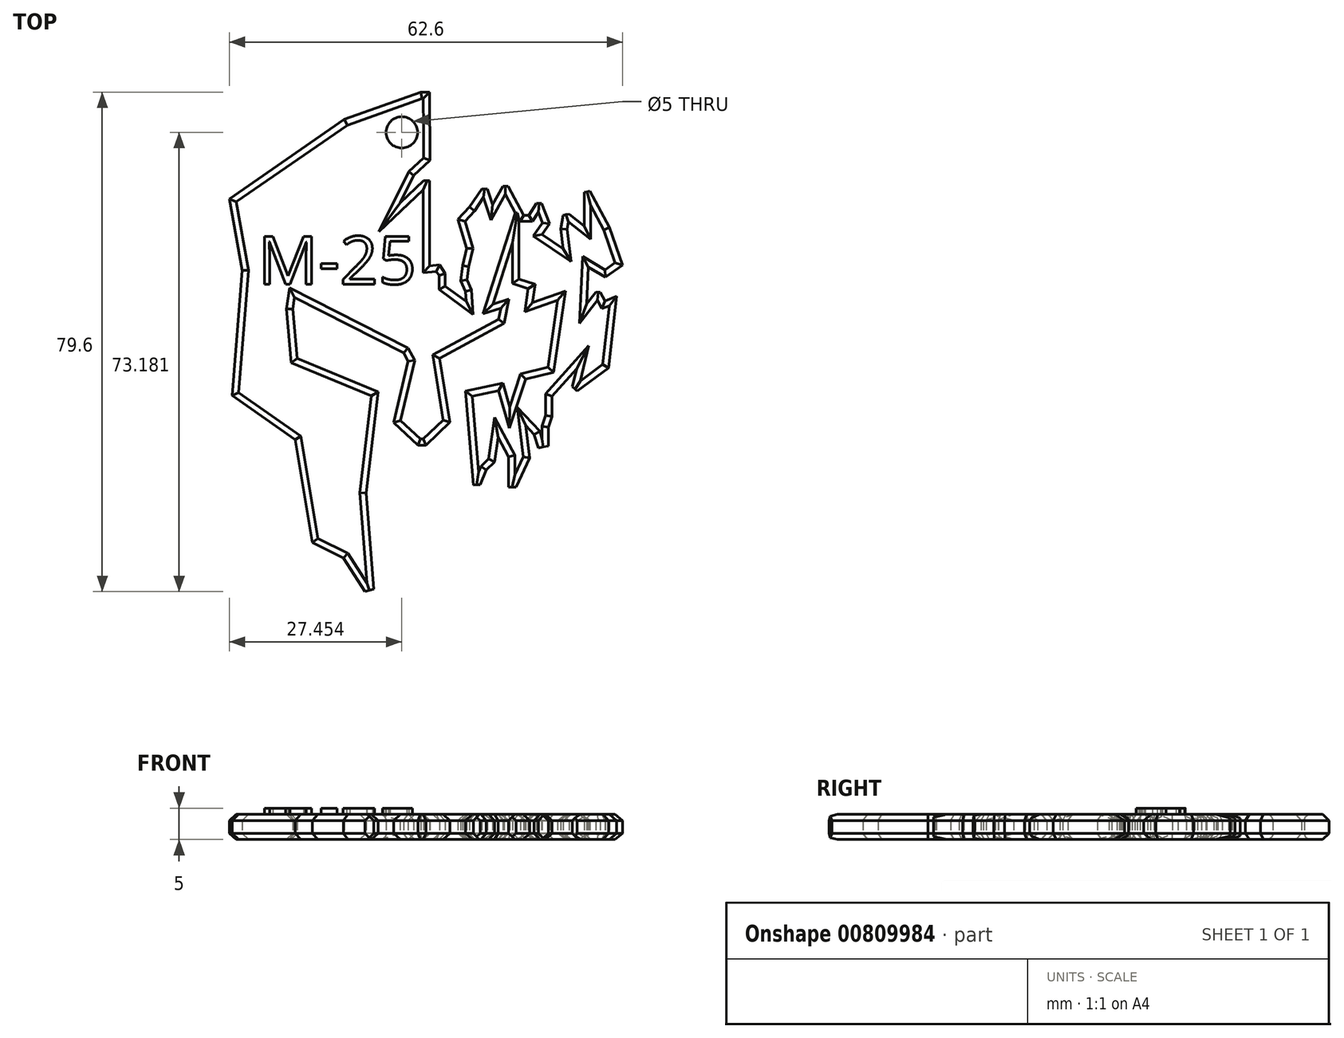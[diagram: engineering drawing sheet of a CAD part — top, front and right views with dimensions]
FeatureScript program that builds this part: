
annotation { "Feature Type Name" : "Feature", "Feature Type Description" : "" }
export const myFeature = defineFeature(function(context is Context, id is Id, definition is map)
    precondition{}
    {
        {
            var Q0;
            Q0=qCreatedBy(makeId("Top.planeOp"),FACE);
            var sketch = newSketch(context, id + "F0", { "sketchPlane" : qUnion([Q0])});
            skLineSegment(sketch, "E0", {"start": v(1.37, 41.13) * mm, "end": v(0, 41.13) * mm});
            skLineSegment(sketch, "E1", {"start": v(0, 41.13) * mm, "end": v(-12.19, 36.77) * mm});
            skLineSegment(sketch, "E2", {"start": v(-12.19, 36.77) * mm, "end": v(-30.5, 24.12) * mm});
            skLineSegment(sketch, "E3", {"start": v(-30.5, 24.12) * mm, "end": v(-28.46, 12.71) * mm});
            skLineSegment(sketch, "E4", {"start": v(-28.46, 12.71) * mm, "end": v(-30.1, -7.22) * mm});
            skLineSegment(sketch, "E5", {"start": v(-30.1, -7.22) * mm, "end": v(-20.03, -14.27) * mm});
            skLineSegment(sketch, "E6", {"start": v(-20.03, -14.27) * mm, "end": v(-17.31, -30.66) * mm});
            skLineSegment(sketch, "E7", {"start": v(-17.31, -30.66) * mm, "end": v(-12.37, -33.1) * mm});
            skLineSegment(sketch, "E8", {"start": v(-12.37, -33.1) * mm, "end": v(-8.91, -38.47) * mm});
            skLineSegment(sketch, "E9", {"start": v(-8.91, -38.47) * mm, "end": v(-7.52, -38.05) * mm});
            skLineSegment(sketch, "E10", {"start": v(-7.52, -38.05) * mm, "end": v(-8.72, -22.74) * mm});
            skLineSegment(sketch, "E11", {"start": v(-8.72, -22.74) * mm, "end": v(-6.8, -6.66) * mm});
            skLineSegment(sketch, "E12", {"start": v(-6.8, -6.66) * mm, "end": v(-19.71, -1.28) * mm});
            skLineSegment(sketch, "E13", {"start": v(-19.71, -1.28) * mm, "end": v(-20.44, 6.56) * mm});
            skLineSegment(sketch, "E14", {"start": v(-20.44, 6.56) * mm, "end": v(-20.14, 8.4) * mm});
            skLineSegment(sketch, "E15", {"start": v(-20.14, 8.4) * mm, "end": v(-2.78, -0.4) * mm});
            skLineSegment(sketch, "E16", {"start": v(-2.78, -0.4) * mm, "end": v(-2.05, -1.73) * mm});
            skLineSegment(sketch, "E17", {"start": v(-2.05, -1.73) * mm, "end": v(-4.36, -11.52) * mm});
            skLineSegment(sketch, "E18", {"start": v(-4.36, -11.52) * mm, "end": v(-0.47, -15.16) * mm});
            skLineSegment(sketch, "E19", {"start": v(-0.47, -15.16) * mm, "end": v(0.77, -15.16) * mm});
            skLineSegment(sketch, "E20", {"start": v(0.77, -15.16) * mm, "end": v(4.58, -11.48) * mm});
            skLineSegment(sketch, "E21", {"start": v(4.58, -11.48) * mm, "end": v(2.95, -1.28) * mm});
            skLineSegment(sketch, "E22", {"start": v(2.95, -1.28) * mm, "end": v(13.28, 4.29) * mm});
            skLineSegment(sketch, "E23", {"start": v(13.28, 4.29) * mm, "end": v(14, 8.17) * mm});
            skLineSegment(sketch, "E24", {"start": v(14, 8.17) * mm, "end": v(11.45, 7.36) * mm});
            skLineSegment(sketch, "E25", {"start": v(11.45, 7.36) * mm, "end": v(14.57, 17.1) * mm});
            skLineSegment(sketch, "E26", {"start": v(14.57, 17.1) * mm, "end": v(14.57, 10.62) * mm});
            skLineSegment(sketch, "E27", {"start": v(14.57, 10.62) * mm, "end": v(17.07, 9.8) * mm});
            skLineSegment(sketch, "E28", {"start": v(17.07, 9.8) * mm, "end": v(16.54, 6.11) * mm});
            skLineSegment(sketch, "E29", {"start": v(16.54, 6.11) * mm, "end": v(21.77, 7.96) * mm});
            skPoint(sketch, "E29.endSnap0", {"position": v(16.8, 7.96) * mm});
            skLineSegment(sketch, "E30", {"start": v(21.77, 7.96) * mm, "end": v(20.25, -2.72) * mm});
            skLineSegment(sketch, "E31", {"start": v(20.25, -2.72) * mm, "end": v(15.87, -3.78) * mm});
            skLineSegment(sketch, "E32", {"start": v(15.87, -3.78) * mm, "end": v(14.14, -9.06) * mm});
            skLineSegment(sketch, "E33", {"start": v(14.14, -9.06) * mm, "end": v(13.04, -5.27) * mm});
            skLineSegment(sketch, "E34", {"start": v(13.04, -5.27) * mm, "end": v(7.08, -6.51) * mm});
            skLineSegment(sketch, "E35", {"start": v(7.08, -6.51) * mm, "end": v(8.37, -21.5) * mm});
            skLineSegment(sketch, "E36", {"start": v(8.37, -21.5) * mm, "end": v(9.44, -21.4) * mm});
            skLineSegment(sketch, "E37", {"start": v(9.44, -21.4) * mm, "end": v(10.38, -19.1) * mm});
            skLineSegment(sketch, "E38", {"start": v(10.38, -19.1) * mm, "end": v(11.73, -17.8) * mm});
            skLineSegment(sketch, "E39", {"start": v(11.73, -17.8) * mm, "end": v(12.28, -13.87) * mm});
            skLineSegment(sketch, "E40", {"start": v(12.28, -13.87) * mm, "end": v(13.97, -17) * mm});
            skLineSegment(sketch, "E41", {"start": v(13.97, -17) * mm, "end": v(13.97, -21.84) * mm});
            skLineSegment(sketch, "E42", {"start": v(13.97, -21.84) * mm, "end": v(15.14, -21.84) * mm});
            skLineSegment(sketch, "E43", {"start": v(15.14, -21.84) * mm, "end": v(17.3, -17.18) * mm});
            skLineSegment(sketch, "E44", {"start": v(17.3, -17.18) * mm, "end": v(16.67, -12) * mm});
            skLineSegment(sketch, "E45", {"start": v(16.67, -12) * mm, "end": v(18.04, -13.44) * mm});
            skLineSegment(sketch, "E46", {"start": v(18.04, -13.44) * mm, "end": v(18.69, -15.57) * mm});
            skLineSegment(sketch, "E47", {"start": v(18.69, -15.57) * mm, "end": v(20.3, -15.28) * mm});
            skLineSegment(sketch, "E48", {"start": v(20.3, -15.28) * mm, "end": v(20.3, -12.26) * mm});
            skLineSegment(sketch, "E49", {"start": v(20.3, -12.26) * mm, "end": v(20.87, -10.56) * mm});
            skLineSegment(sketch, "E50", {"start": v(20.87, -10.56) * mm, "end": v(20.87, -7.35) * mm});
            skLineSegment(sketch, "E51", {"start": v(20.87, -7.35) * mm, "end": v(24.8, -2.92) * mm});
            skLineSegment(sketch, "E52", {"start": v(24.8, -2.92) * mm, "end": v(24.12, -5.8) * mm});
            skLineSegment(sketch, "E53", {"start": v(24.12, -5.8) * mm, "end": v(24.89, -6.51) * mm});
            skLineSegment(sketch, "E54", {"start": v(24.89, -6.51) * mm, "end": v(29.9, -2.8) * mm});
            skLineSegment(sketch, "E55", {"start": v(29.9, -2.8) * mm, "end": v(31.16, 8.57) * mm});
            skLineSegment(sketch, "E56", {"start": v(31.16, 8.57) * mm, "end": v(29.3, 7.85) * mm});
            skLineSegment(sketch, "E57", {"start": v(29.3, 7.85) * mm, "end": v(28.54, 9.24) * mm});
            skLineSegment(sketch, "E58", {"start": v(28.54, 9.24) * mm, "end": v(27.85, 9.24) * mm});
            skLineSegment(sketch, "E59", {"start": v(27.85, 9.24) * mm, "end": v(26.39, 7.37) * mm});
            skLineSegment(sketch, "E60", {"start": v(26.39, 7.37) * mm, "end": v(26.67, 13.25) * mm});
            skLineSegment(sketch, "E61", {"start": v(26.67, 13.25) * mm, "end": v(29.36, 11.62) * mm});
            skLineSegment(sketch, "E62", {"start": v(29.36, 11.62) * mm, "end": v(32.1, 13.54) * mm});
            skLineSegment(sketch, "E63", {"start": v(32.1, 13.54) * mm, "end": v(30.02, 19.57) * mm});
            skLineSegment(sketch, "E64", {"start": v(30.02, 19.57) * mm, "end": v(26.88, 25.4) * mm});
            skLineSegment(sketch, "E65", {"start": v(26.88, 25.4) * mm, "end": v(26, 25.15) * mm});
            skLineSegment(sketch, "E66", {"start": v(26, 25.15) * mm, "end": v(26, 19.79) * mm});
            skLineSegment(sketch, "E67", {"start": v(26, 19.79) * mm, "end": v(23.6, 21.7) * mm});
            skLineSegment(sketch, "E68", {"start": v(23.6, 21.7) * mm, "end": v(22.64, 21.52) * mm});
            skLineSegment(sketch, "E69", {"start": v(22.64, 21.52) * mm, "end": v(22.28, 19.32) * mm});
            skLineSegment(sketch, "E70", {"start": v(22.28, 19.32) * mm, "end": v(22.64, 16.17) * mm});
            skLineSegment(sketch, "E71", {"start": v(22.64, 16.17) * mm, "end": v(19.29, 18.44) * mm});
            skLineSegment(sketch, "E72", {"start": v(19.29, 18.44) * mm, "end": v(20.46, 20.17) * mm});
            skLineSegment(sketch, "E73", {"start": v(20.46, 20.17) * mm, "end": v(19.22, 23.42) * mm});
            skLineSegment(sketch, "E74", {"start": v(19.22, 23.42) * mm, "end": v(18.39, 23.42) * mm});
            skLineSegment(sketch, "E75", {"start": v(18.39, 23.42) * mm, "end": v(17.21, 21.52) * mm});
            skLineSegment(sketch, "E76", {"start": v(17.21, 21.52) * mm, "end": v(16.38, 21.52) * mm});
            skLineSegment(sketch, "E77", {"start": v(16.38, 21.52) * mm, "end": v(13.88, 26.15) * mm});
            skLineSegment(sketch, "E78", {"start": v(13.88, 26.15) * mm, "end": v(13.04, 26.15) * mm});
            skLineSegment(sketch, "E79", {"start": v(13.04, 26.15) * mm, "end": v(11.39, 23.2) * mm});
            skLineSegment(sketch, "E80", {"start": v(11.39, 23.2) * mm, "end": v(10.57, 25.7) * mm});
            skLineSegment(sketch, "E81", {"start": v(10.57, 25.7) * mm, "end": v(9.66, 25.68) * mm});
            skLineSegment(sketch, "E82", {"start": v(9.66, 25.68) * mm, "end": v(7.74, 22.8) * mm});
            skLineSegment(sketch, "E83", {"start": v(7.74, 22.8) * mm, "end": v(5.87, 20.83) * mm});
            skLineSegment(sketch, "E84", {"start": v(5.87, 20.83) * mm, "end": v(7.26, 16.2) * mm});
            skLineSegment(sketch, "E85", {"start": v(7.26, 16.2) * mm, "end": v(6.61, 13.46) * mm});
            skLineSegment(sketch, "E86", {"start": v(6.61, 13.46) * mm, "end": v(6.3, 11.06) * mm});
            skLineSegment(sketch, "E87", {"start": v(6.3, 11.06) * mm, "end": v(7.08, 9.38) * mm});
            skLineSegment(sketch, "E88", {"start": v(7.08, 9.38) * mm, "end": v(7.18, 7.76) * mm});
            skLineSegment(sketch, "E89", {"start": v(7.18, 7.76) * mm, "end": v(3.87, 10.2) * mm});
            skLineSegment(sketch, "E90", {"start": v(3.87, 10.2) * mm, "end": v(3.87, 12.24) * mm});
            skLineSegment(sketch, "E91", {"start": v(3.87, 12.24) * mm, "end": v(2.95, 13.63) * mm});
            skLineSegment(sketch, "E92", {"start": v(2.95, 13.63) * mm, "end": v(1.35, 13.46) * mm});
            skLineSegment(sketch, "E93", {"start": v(1.35, 13.46) * mm, "end": v(1.35, 27.03) * mm});
            skLineSegment(sketch, "E94", {"start": v(1.35, 27.03) * mm, "end": v(0.44, 27.03) * mm});
            skLineSegment(sketch, "E95", {"start": v(0.44, 27.03) * mm, "end": v(-3.3, 23.47) * mm});
            skLineSegment(sketch, "E96", {"start": v(-3.3, 23.47) * mm, "end": v(-1.14, 27.85) * mm});
            skLineSegment(sketch, "E97", {"start": v(-1.14, 27.85) * mm, "end": v(1.41, 30.23) * mm});
            skLineSegment(sketch, "E98", {"start": v(1.41, 30.23) * mm, "end": v(1.37, 41.13) * mm});
            skCircle(sketch, "E99", {"center": v(-3.05, 34.71) * mm, "radius": 2.5 * mm});
            skSolve(sketch);
        }
        {
            var Q0;
            Q0=makeQuery(id+"F0.imprint","IMPRINT",FACE,{"disambiguationData":[TD([[makeQuery(id+"F0.imprint","IMPRINT",EDGE,{"derivedFrom":sQuery(id+"F0.wireOp",EDGE,"E0")}),1.0]])]});
            extrude(context, id + "F1", {"entities" : qUnion([Q0]), "depth" : 4 * mm, "offsetDistance" : 25 * mm});
        }
        {
            var Q0;
            Q0=makeQuery(id+"F1.opExtrude","CAP_EDGE",EDGE,{"disambiguationData":[OSD([sQuery(id+"F0.wireOp",EDGE,"E99")])],"isStart":true});
            var Q1;
            Q1=makeQuery(id+"F1.opExtrude","CAP_EDGE",EDGE,{"disambiguationData":[OSD([sQuery(id+"F0.wireOp",EDGE,"E99")])],"isStart":false});
            fillet(context, id + "F2", {"entities" : qUnion([Q0, Q1]), "radius" : 1 * mm, "tangentPropagation" : true, "allowEdgeOverflow" : false});
        }
        {
            var Q0;
            Q0=makeQuery(id+"F1.opExtrude","CAP_FACE",FACE,{"disambiguationData":[OSD([sQuery(id+"F0.wireOp",EDGE,"E0"),sQuery(id+"F0.wireOp",EDGE,"E1"),sQuery(id+"F0.wireOp",EDGE,"E2"),sQuery(id+"F0.wireOp",EDGE,"E3"),sQuery(id+"F0.wireOp",EDGE,"E4"),sQuery(id+"F0.wireOp",EDGE,"E5"),sQuery(id+"F0.wireOp",EDGE,"E6"),sQuery(id+"F0.wireOp",EDGE,"E7"),sQuery(id+"F0.wireOp",EDGE,"E8"),sQuery(id+"F0.wireOp",EDGE,"E9"),sQuery(id+"F0.wireOp",EDGE,"E10"),sQuery(id+"F0.wireOp",EDGE,"E11"),sQuery(id+"F0.wireOp",EDGE,"E12"),sQuery(id+"F0.wireOp",EDGE,"E13"),sQuery(id+"F0.wireOp",EDGE,"E14"),sQuery(id+"F0.wireOp",EDGE,"E15"),sQuery(id+"F0.wireOp",EDGE,"E16"),sQuery(id+"F0.wireOp",EDGE,"E17"),sQuery(id+"F0.wireOp",EDGE,"E18"),sQuery(id+"F0.wireOp",EDGE,"E19"),sQuery(id+"F0.wireOp",EDGE,"E20"),sQuery(id+"F0.wireOp",EDGE,"E21"),sQuery(id+"F0.wireOp",EDGE,"E22"),sQuery(id+"F0.wireOp",EDGE,"E23"),sQuery(id+"F0.wireOp",EDGE,"E24"),sQuery(id+"F0.wireOp",EDGE,"E25"),sQuery(id+"F0.wireOp",EDGE,"E26"),sQuery(id+"F0.wireOp",EDGE,"E27"),sQuery(id+"F0.wireOp",EDGE,"E28"),sQuery(id+"F0.wireOp",EDGE,"E29"),sQuery(id+"F0.wireOp",EDGE,"E30"),sQuery(id+"F0.wireOp",EDGE,"E31"),sQuery(id+"F0.wireOp",EDGE,"E32"),sQuery(id+"F0.wireOp",EDGE,"E33"),sQuery(id+"F0.wireOp",EDGE,"E34"),sQuery(id+"F0.wireOp",EDGE,"E35"),sQuery(id+"F0.wireOp",EDGE,"E36"),sQuery(id+"F0.wireOp",EDGE,"E37"),sQuery(id+"F0.wireOp",EDGE,"E38"),sQuery(id+"F0.wireOp",EDGE,"E39"),sQuery(id+"F0.wireOp",EDGE,"E40"),sQuery(id+"F0.wireOp",EDGE,"E41"),sQuery(id+"F0.wireOp",EDGE,"E42"),sQuery(id+"F0.wireOp",EDGE,"E43"),sQuery(id+"F0.wireOp",EDGE,"E44"),sQuery(id+"F0.wireOp",EDGE,"E45"),sQuery(id+"F0.wireOp",EDGE,"E46"),sQuery(id+"F0.wireOp",EDGE,"E47"),sQuery(id+"F0.wireOp",EDGE,"E48"),sQuery(id+"F0.wireOp",EDGE,"E49"),sQuery(id+"F0.wireOp",EDGE,"E50"),sQuery(id+"F0.wireOp",EDGE,"E51"),sQuery(id+"F0.wireOp",EDGE,"E52"),sQuery(id+"F0.wireOp",EDGE,"E53"),sQuery(id+"F0.wireOp",EDGE,"E54"),sQuery(id+"F0.wireOp",EDGE,"E55"),sQuery(id+"F0.wireOp",EDGE,"E56"),sQuery(id+"F0.wireOp",EDGE,"E57"),sQuery(id+"F0.wireOp",EDGE,"E58"),sQuery(id+"F0.wireOp",EDGE,"E59"),sQuery(id+"F0.wireOp",EDGE,"E60"),sQuery(id+"F0.wireOp",EDGE,"E61"),sQuery(id+"F0.wireOp",EDGE,"E62"),sQuery(id+"F0.wireOp",EDGE,"E63"),sQuery(id+"F0.wireOp",EDGE,"E64"),sQuery(id+"F0.wireOp",EDGE,"E65"),sQuery(id+"F0.wireOp",EDGE,"E66"),sQuery(id+"F0.wireOp",EDGE,"E67"),sQuery(id+"F0.wireOp",EDGE,"E68"),sQuery(id+"F0.wireOp",EDGE,"E69"),sQuery(id+"F0.wireOp",EDGE,"E70"),sQuery(id+"F0.wireOp",EDGE,"E71"),sQuery(id+"F0.wireOp",EDGE,"E72"),sQuery(id+"F0.wireOp",EDGE,"E73"),sQuery(id+"F0.wireOp",EDGE,"E74"),sQuery(id+"F0.wireOp",EDGE,"E75"),sQuery(id+"F0.wireOp",EDGE,"E76"),sQuery(id+"F0.wireOp",EDGE,"E77"),sQuery(id+"F0.wireOp",EDGE,"E78"),sQuery(id+"F0.wireOp",EDGE,"E79"),sQuery(id+"F0.wireOp",EDGE,"E80"),sQuery(id+"F0.wireOp",EDGE,"E81"),sQuery(id+"F0.wireOp",EDGE,"E82"),sQuery(id+"F0.wireOp",EDGE,"E83"),sQuery(id+"F0.wireOp",EDGE,"E84"),sQuery(id+"F0.wireOp",EDGE,"E85"),sQuery(id+"F0.wireOp",EDGE,"E86"),sQuery(id+"F0.wireOp",EDGE,"E87"),sQuery(id+"F0.wireOp",EDGE,"E88"),sQuery(id+"F0.wireOp",EDGE,"E89"),sQuery(id+"F0.wireOp",EDGE,"E90"),sQuery(id+"F0.wireOp",EDGE,"E91"),sQuery(id+"F0.wireOp",EDGE,"E92"),sQuery(id+"F0.wireOp",EDGE,"E93"),sQuery(id+"F0.wireOp",EDGE,"E94"),sQuery(id+"F0.wireOp",EDGE,"E95"),sQuery(id+"F0.wireOp",EDGE,"E96"),sQuery(id+"F0.wireOp",EDGE,"E97"),sQuery(id+"F0.wireOp",EDGE,"E98"),sQuery(id+"F0.wireOp",EDGE,"E99")])],"isStart":false});
            var Q1;
            Q1=makeQuery(id+"F1.opExtrude","CAP_FACE",FACE,{"disambiguationData":[OSD([sQuery(id+"F0.wireOp",EDGE,"E0"),sQuery(id+"F0.wireOp",EDGE,"E1"),sQuery(id+"F0.wireOp",EDGE,"E2"),sQuery(id+"F0.wireOp",EDGE,"E3"),sQuery(id+"F0.wireOp",EDGE,"E4"),sQuery(id+"F0.wireOp",EDGE,"E5"),sQuery(id+"F0.wireOp",EDGE,"E6"),sQuery(id+"F0.wireOp",EDGE,"E7"),sQuery(id+"F0.wireOp",EDGE,"E8"),sQuery(id+"F0.wireOp",EDGE,"E9"),sQuery(id+"F0.wireOp",EDGE,"E10"),sQuery(id+"F0.wireOp",EDGE,"E11"),sQuery(id+"F0.wireOp",EDGE,"E12"),sQuery(id+"F0.wireOp",EDGE,"E13"),sQuery(id+"F0.wireOp",EDGE,"E14"),sQuery(id+"F0.wireOp",EDGE,"E15"),sQuery(id+"F0.wireOp",EDGE,"E16"),sQuery(id+"F0.wireOp",EDGE,"E17"),sQuery(id+"F0.wireOp",EDGE,"E18"),sQuery(id+"F0.wireOp",EDGE,"E19"),sQuery(id+"F0.wireOp",EDGE,"E20"),sQuery(id+"F0.wireOp",EDGE,"E21"),sQuery(id+"F0.wireOp",EDGE,"E22"),sQuery(id+"F0.wireOp",EDGE,"E23"),sQuery(id+"F0.wireOp",EDGE,"E24"),sQuery(id+"F0.wireOp",EDGE,"E25"),sQuery(id+"F0.wireOp",EDGE,"E26"),sQuery(id+"F0.wireOp",EDGE,"E27"),sQuery(id+"F0.wireOp",EDGE,"E28"),sQuery(id+"F0.wireOp",EDGE,"E29"),sQuery(id+"F0.wireOp",EDGE,"E30"),sQuery(id+"F0.wireOp",EDGE,"E31"),sQuery(id+"F0.wireOp",EDGE,"E32"),sQuery(id+"F0.wireOp",EDGE,"E33"),sQuery(id+"F0.wireOp",EDGE,"E34"),sQuery(id+"F0.wireOp",EDGE,"E35"),sQuery(id+"F0.wireOp",EDGE,"E36"),sQuery(id+"F0.wireOp",EDGE,"E37"),sQuery(id+"F0.wireOp",EDGE,"E38"),sQuery(id+"F0.wireOp",EDGE,"E39"),sQuery(id+"F0.wireOp",EDGE,"E40"),sQuery(id+"F0.wireOp",EDGE,"E41"),sQuery(id+"F0.wireOp",EDGE,"E42"),sQuery(id+"F0.wireOp",EDGE,"E43"),sQuery(id+"F0.wireOp",EDGE,"E44"),sQuery(id+"F0.wireOp",EDGE,"E45"),sQuery(id+"F0.wireOp",EDGE,"E46"),sQuery(id+"F0.wireOp",EDGE,"E47"),sQuery(id+"F0.wireOp",EDGE,"E48"),sQuery(id+"F0.wireOp",EDGE,"E49"),sQuery(id+"F0.wireOp",EDGE,"E50"),sQuery(id+"F0.wireOp",EDGE,"E51"),sQuery(id+"F0.wireOp",EDGE,"E52"),sQuery(id+"F0.wireOp",EDGE,"E53"),sQuery(id+"F0.wireOp",EDGE,"E54"),sQuery(id+"F0.wireOp",EDGE,"E55"),sQuery(id+"F0.wireOp",EDGE,"E56"),sQuery(id+"F0.wireOp",EDGE,"E57"),sQuery(id+"F0.wireOp",EDGE,"E58"),sQuery(id+"F0.wireOp",EDGE,"E59"),sQuery(id+"F0.wireOp",EDGE,"E60"),sQuery(id+"F0.wireOp",EDGE,"E61"),sQuery(id+"F0.wireOp",EDGE,"E62"),sQuery(id+"F0.wireOp",EDGE,"E63"),sQuery(id+"F0.wireOp",EDGE,"E64"),sQuery(id+"F0.wireOp",EDGE,"E65"),sQuery(id+"F0.wireOp",EDGE,"E66"),sQuery(id+"F0.wireOp",EDGE,"E67"),sQuery(id+"F0.wireOp",EDGE,"E68"),sQuery(id+"F0.wireOp",EDGE,"E69"),sQuery(id+"F0.wireOp",EDGE,"E70"),sQuery(id+"F0.wireOp",EDGE,"E71"),sQuery(id+"F0.wireOp",EDGE,"E72"),sQuery(id+"F0.wireOp",EDGE,"E73"),sQuery(id+"F0.wireOp",EDGE,"E74"),sQuery(id+"F0.wireOp",EDGE,"E75"),sQuery(id+"F0.wireOp",EDGE,"E76"),sQuery(id+"F0.wireOp",EDGE,"E77"),sQuery(id+"F0.wireOp",EDGE,"E78"),sQuery(id+"F0.wireOp",EDGE,"E79"),sQuery(id+"F0.wireOp",EDGE,"E80"),sQuery(id+"F0.wireOp",EDGE,"E81"),sQuery(id+"F0.wireOp",EDGE,"E82"),sQuery(id+"F0.wireOp",EDGE,"E83"),sQuery(id+"F0.wireOp",EDGE,"E84"),sQuery(id+"F0.wireOp",EDGE,"E85"),sQuery(id+"F0.wireOp",EDGE,"E86"),sQuery(id+"F0.wireOp",EDGE,"E87"),sQuery(id+"F0.wireOp",EDGE,"E88"),sQuery(id+"F0.wireOp",EDGE,"E89"),sQuery(id+"F0.wireOp",EDGE,"E90"),sQuery(id+"F0.wireOp",EDGE,"E91"),sQuery(id+"F0.wireOp",EDGE,"E92"),sQuery(id+"F0.wireOp",EDGE,"E93"),sQuery(id+"F0.wireOp",EDGE,"E94"),sQuery(id+"F0.wireOp",EDGE,"E95"),sQuery(id+"F0.wireOp",EDGE,"E96"),sQuery(id+"F0.wireOp",EDGE,"E97"),sQuery(id+"F0.wireOp",EDGE,"E98"),sQuery(id+"F0.wireOp",EDGE,"E99")])],"isStart":true});
            chamfer(context, id + "F3", {"entities" : qUnion([Q0, Q1]), "width" : 1 * mm, "tangentPropagation" : true});
        }
        {
            var Q0;
            Q0=makeQuery(id+"F3.opChamfer","SPLIT",FACE,{"disambiguationData":[OD(1.0)],"derivedFrom":makeQuery(id+"F1.opExtrude","CAP_FACE",FACE,{"disambiguationData":[OSD([sQuery(id+"F0.wireOp",EDGE,"E0"),sQuery(id+"F0.wireOp",EDGE,"E1"),sQuery(id+"F0.wireOp",EDGE,"E2"),sQuery(id+"F0.wireOp",EDGE,"E3"),sQuery(id+"F0.wireOp",EDGE,"E4"),sQuery(id+"F0.wireOp",EDGE,"E5"),sQuery(id+"F0.wireOp",EDGE,"E6"),sQuery(id+"F0.wireOp",EDGE,"E7"),sQuery(id+"F0.wireOp",EDGE,"E8"),sQuery(id+"F0.wireOp",EDGE,"E9"),sQuery(id+"F0.wireOp",EDGE,"E10"),sQuery(id+"F0.wireOp",EDGE,"E11"),sQuery(id+"F0.wireOp",EDGE,"E12"),sQuery(id+"F0.wireOp",EDGE,"E13"),sQuery(id+"F0.wireOp",EDGE,"E14"),sQuery(id+"F0.wireOp",EDGE,"E15"),sQuery(id+"F0.wireOp",EDGE,"E16"),sQuery(id+"F0.wireOp",EDGE,"E17"),sQuery(id+"F0.wireOp",EDGE,"E18"),sQuery(id+"F0.wireOp",EDGE,"E19"),sQuery(id+"F0.wireOp",EDGE,"E20"),sQuery(id+"F0.wireOp",EDGE,"E21"),sQuery(id+"F0.wireOp",EDGE,"E22"),sQuery(id+"F0.wireOp",EDGE,"E23"),sQuery(id+"F0.wireOp",EDGE,"E24"),sQuery(id+"F0.wireOp",EDGE,"E25"),sQuery(id+"F0.wireOp",EDGE,"E26"),sQuery(id+"F0.wireOp",EDGE,"E27"),sQuery(id+"F0.wireOp",EDGE,"E28"),sQuery(id+"F0.wireOp",EDGE,"E29"),sQuery(id+"F0.wireOp",EDGE,"E30"),sQuery(id+"F0.wireOp",EDGE,"E31"),sQuery(id+"F0.wireOp",EDGE,"E32"),sQuery(id+"F0.wireOp",EDGE,"E33"),sQuery(id+"F0.wireOp",EDGE,"E34"),sQuery(id+"F0.wireOp",EDGE,"E35"),sQuery(id+"F0.wireOp",EDGE,"E36"),sQuery(id+"F0.wireOp",EDGE,"E37"),sQuery(id+"F0.wireOp",EDGE,"E38"),sQuery(id+"F0.wireOp",EDGE,"E39"),sQuery(id+"F0.wireOp",EDGE,"E40"),sQuery(id+"F0.wireOp",EDGE,"E41"),sQuery(id+"F0.wireOp",EDGE,"E42"),sQuery(id+"F0.wireOp",EDGE,"E43"),sQuery(id+"F0.wireOp",EDGE,"E44"),sQuery(id+"F0.wireOp",EDGE,"E45"),sQuery(id+"F0.wireOp",EDGE,"E46"),sQuery(id+"F0.wireOp",EDGE,"E47"),sQuery(id+"F0.wireOp",EDGE,"E48"),sQuery(id+"F0.wireOp",EDGE,"E49"),sQuery(id+"F0.wireOp",EDGE,"E50"),sQuery(id+"F0.wireOp",EDGE,"E51"),sQuery(id+"F0.wireOp",EDGE,"E52"),sQuery(id+"F0.wireOp",EDGE,"E53"),sQuery(id+"F0.wireOp",EDGE,"E54"),sQuery(id+"F0.wireOp",EDGE,"E55"),sQuery(id+"F0.wireOp",EDGE,"E56"),sQuery(id+"F0.wireOp",EDGE,"E57"),sQuery(id+"F0.wireOp",EDGE,"E58"),sQuery(id+"F0.wireOp",EDGE,"E59"),sQuery(id+"F0.wireOp",EDGE,"E60"),sQuery(id+"F0.wireOp",EDGE,"E61"),sQuery(id+"F0.wireOp",EDGE,"E62"),sQuery(id+"F0.wireOp",EDGE,"E63"),sQuery(id+"F0.wireOp",EDGE,"E64"),sQuery(id+"F0.wireOp",EDGE,"E65"),sQuery(id+"F0.wireOp",EDGE,"E66"),sQuery(id+"F0.wireOp",EDGE,"E67"),sQuery(id+"F0.wireOp",EDGE,"E68"),sQuery(id+"F0.wireOp",EDGE,"E69"),sQuery(id+"F0.wireOp",EDGE,"E70"),sQuery(id+"F0.wireOp",EDGE,"E71"),sQuery(id+"F0.wireOp",EDGE,"E72"),sQuery(id+"F0.wireOp",EDGE,"E73"),sQuery(id+"F0.wireOp",EDGE,"E74"),sQuery(id+"F0.wireOp",EDGE,"E75"),sQuery(id+"F0.wireOp",EDGE,"E76"),sQuery(id+"F0.wireOp",EDGE,"E77"),sQuery(id+"F0.wireOp",EDGE,"E78"),sQuery(id+"F0.wireOp",EDGE,"E79"),sQuery(id+"F0.wireOp",EDGE,"E80"),sQuery(id+"F0.wireOp",EDGE,"E81"),sQuery(id+"F0.wireOp",EDGE,"E82"),sQuery(id+"F0.wireOp",EDGE,"E83"),sQuery(id+"F0.wireOp",EDGE,"E84"),sQuery(id+"F0.wireOp",EDGE,"E85"),sQuery(id+"F0.wireOp",EDGE,"E86"),sQuery(id+"F0.wireOp",EDGE,"E87"),sQuery(id+"F0.wireOp",EDGE,"E88"),sQuery(id+"F0.wireOp",EDGE,"E89"),sQuery(id+"F0.wireOp",EDGE,"E90"),sQuery(id+"F0.wireOp",EDGE,"E91"),sQuery(id+"F0.wireOp",EDGE,"E92"),sQuery(id+"F0.wireOp",EDGE,"E93"),sQuery(id+"F0.wireOp",EDGE,"E94"),sQuery(id+"F0.wireOp",EDGE,"E95"),sQuery(id+"F0.wireOp",EDGE,"E96"),sQuery(id+"F0.wireOp",EDGE,"E97"),sQuery(id+"F0.wireOp",EDGE,"E98"),sQuery(id+"F0.wireOp",EDGE,"E99")])],"isStart":false})});
            var sketch = newSketch(context, id + "F4", { "sketchPlane" : qUnion([Q0])});
            skText(sketch, "E100", { "text": "M-25", "fontName": "OpenSans-Regular.ttf"});
            skPoint(sketch, "E100.secondSnap0", {"position": v(-28.43, 18.21) * mm});
            const initialGuessF4  = {"E100": [-0.02598, 0.01054, 1, 0, 0.00767]};
            skSetInitialGuess(sketch, initialGuessF4);
            skSolve(sketch);
        }
        {
            var Q0;
            Q0 = qSketchRegion(id + "F4", true);
            extrude(context, id + "F5", {"entities" : qUnion([Q0]), "operationType" : NewBodyOperationType.ADD, "depth" : 1 * mm, "offsetDistance" : 25 * mm});
        }
    });
